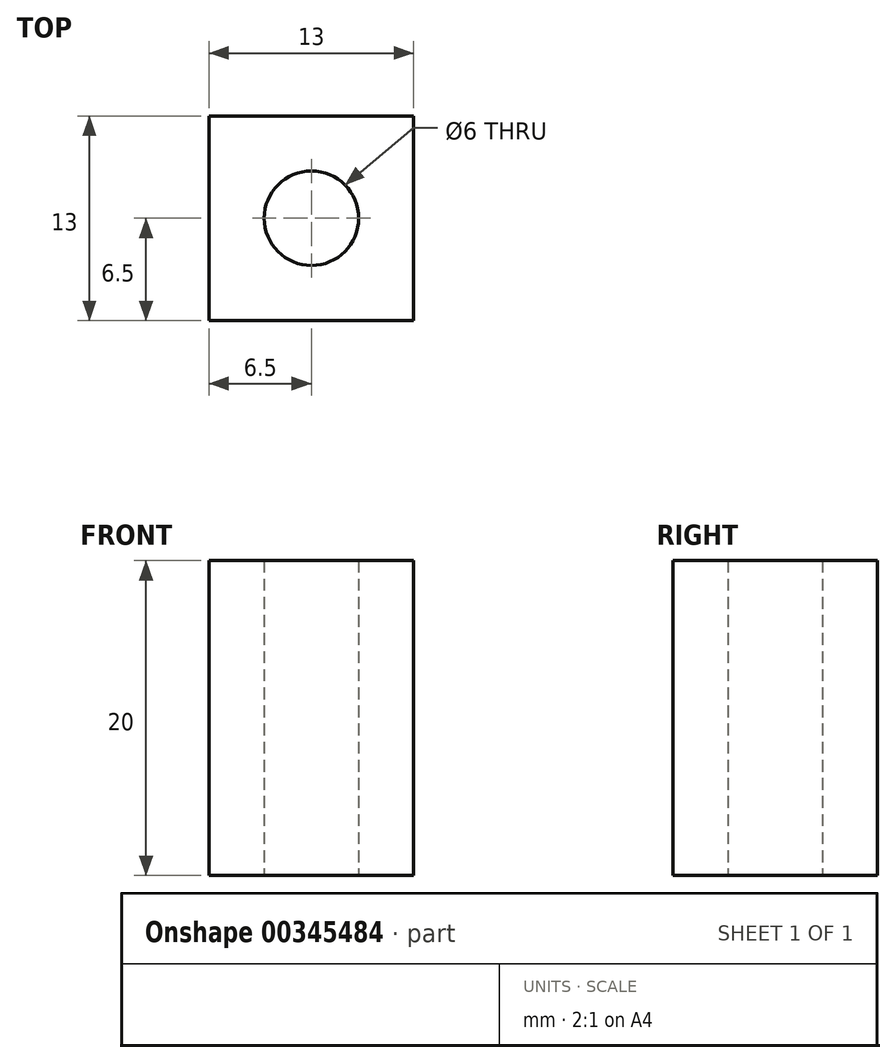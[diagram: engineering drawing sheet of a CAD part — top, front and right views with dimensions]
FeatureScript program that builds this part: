
annotation { "Feature Type Name" : "Feature", "Feature Type Description" : "" }
export const myFeature = defineFeature(function(context is Context, id is Id, definition is map)
    precondition{}
    {
        {
            var Q0;
            Q0=qCreatedBy(makeId("Top.planeOp"),FACE);
            var sketch = newSketch(context, id + "F0", { "sketchPlane" : qUnion([Q0])});
            skLineSegment(sketch, "E0.bottom", {"start": v(6.5, -6.5) * mm, "end": v(-6.5, -6.5) * mm});
            skLineSegment(sketch, "E0.top", {"start": v(6.5, 6.5) * mm, "end": v(-6.5, 6.5) * mm});
            skLineSegment(sketch, "E0.left", {"start": v(6.5, -6.5) * mm, "end": v(6.5, 6.5) * mm});
            skLineSegment(sketch, "E0.right", {"start": v(-6.5, -6.5) * mm, "end": v(-6.5, 6.5) * mm});
            skPoint(sketch, "E0.middle", {"position": v(0, 0) * mm});
            skCircle(sketch, "E1", {"center": v(0, 0) * mm, "radius": 3 * mm});
            skSolve(sketch);
        }
        {
            var Q0;
            Q0=makeQuery(id+"F0.imprint","IMPRINT",FACE,{"disambiguationData":[TD([[makeQuery(id+"F0.imprint","IMPRINT",EDGE,{"derivedFrom":sQuery(id+"F0.wireOp",EDGE,"E0.bottom")}),-1.0]])]});
            extrude(context, id + "F1", {"entities" : qUnion([Q0]), "depth" : 20 * mm});
        }
    });
